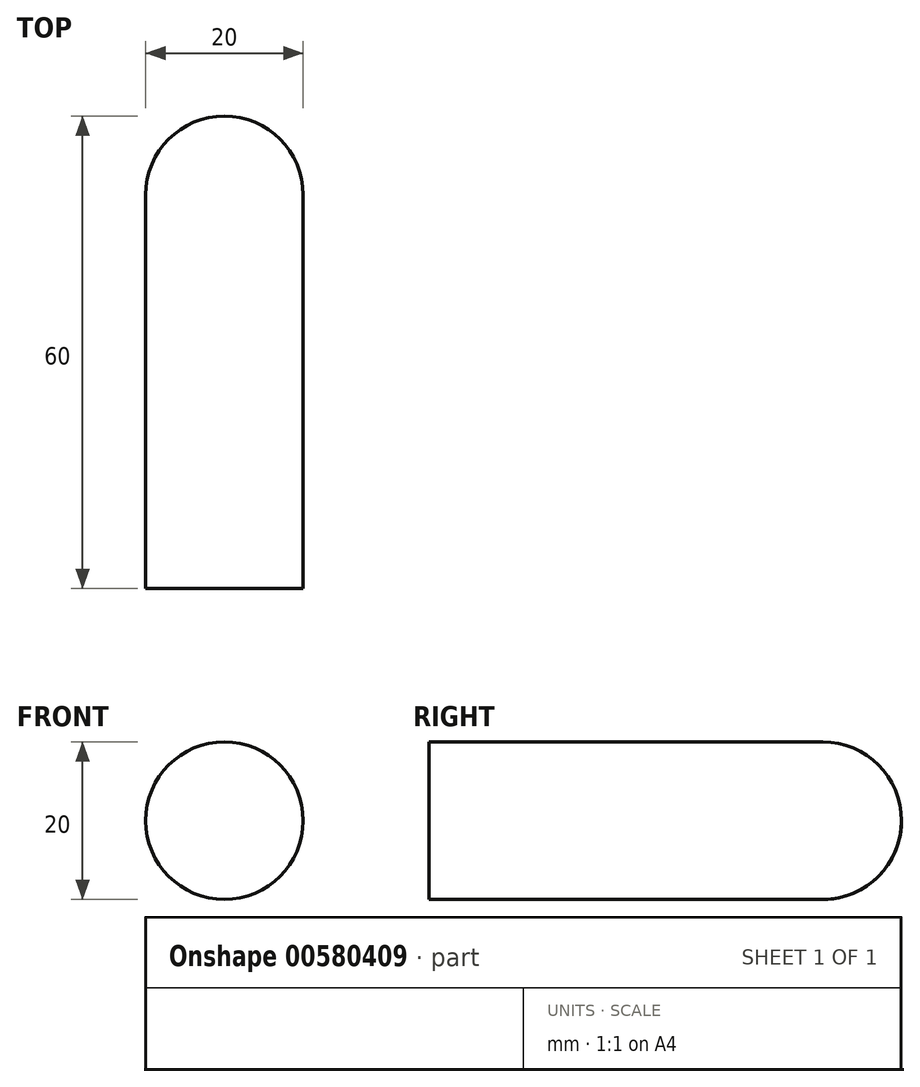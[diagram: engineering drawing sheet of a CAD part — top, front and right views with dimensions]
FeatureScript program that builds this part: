
annotation { "Feature Type Name" : "Feature", "Feature Type Description" : "" }
export const myFeature = defineFeature(function(context is Context, id is Id, definition is map)
    precondition{}
    {
        {
            var Q0;
            Q0=qCreatedBy(makeId("Front.planeOp"),FACE);
            var sketch = newSketch(context, id + "F0", { "sketchPlane" : qUnion([Q0])});
            skCircle(sketch, "E0", {"center": v(0, 0) * mm, "radius": 10 * mm});
            skSolve(sketch);
        }
        {
            var Q0;
            Q0=makeQuery(id+"F0.imprint","IMPRINT",FACE,{"disambiguationData":[TD([[makeQuery(id+"F0.imprint","IMPRINT",EDGE,{"derivedFrom":sQuery(id+"F0.wireOp",EDGE,"E0")}),1.0]])]});
            extrude(context, id + "F1", {"entities" : qUnion([Q0]), "endBound" : BoundingType.SYMMETRIC, "depth" : 60 * mm, "offsetDistance" : 25.4 * mm});
        }
        {
            var Q0;
            Q0=makeQuery(id+"F1.opExtrude","CAP_EDGE",EDGE,{"disambiguationData":[OSD([sQuery(id+"F0.wireOp",EDGE,"E0")])],"isStart":true});
            fillet(context, id + "F2", {"entities" : qUnion([Q0]), "radius" : 10 * mm, "tangentPropagation" : true, "allowEdgeOverflow" : false});
        }
    });
